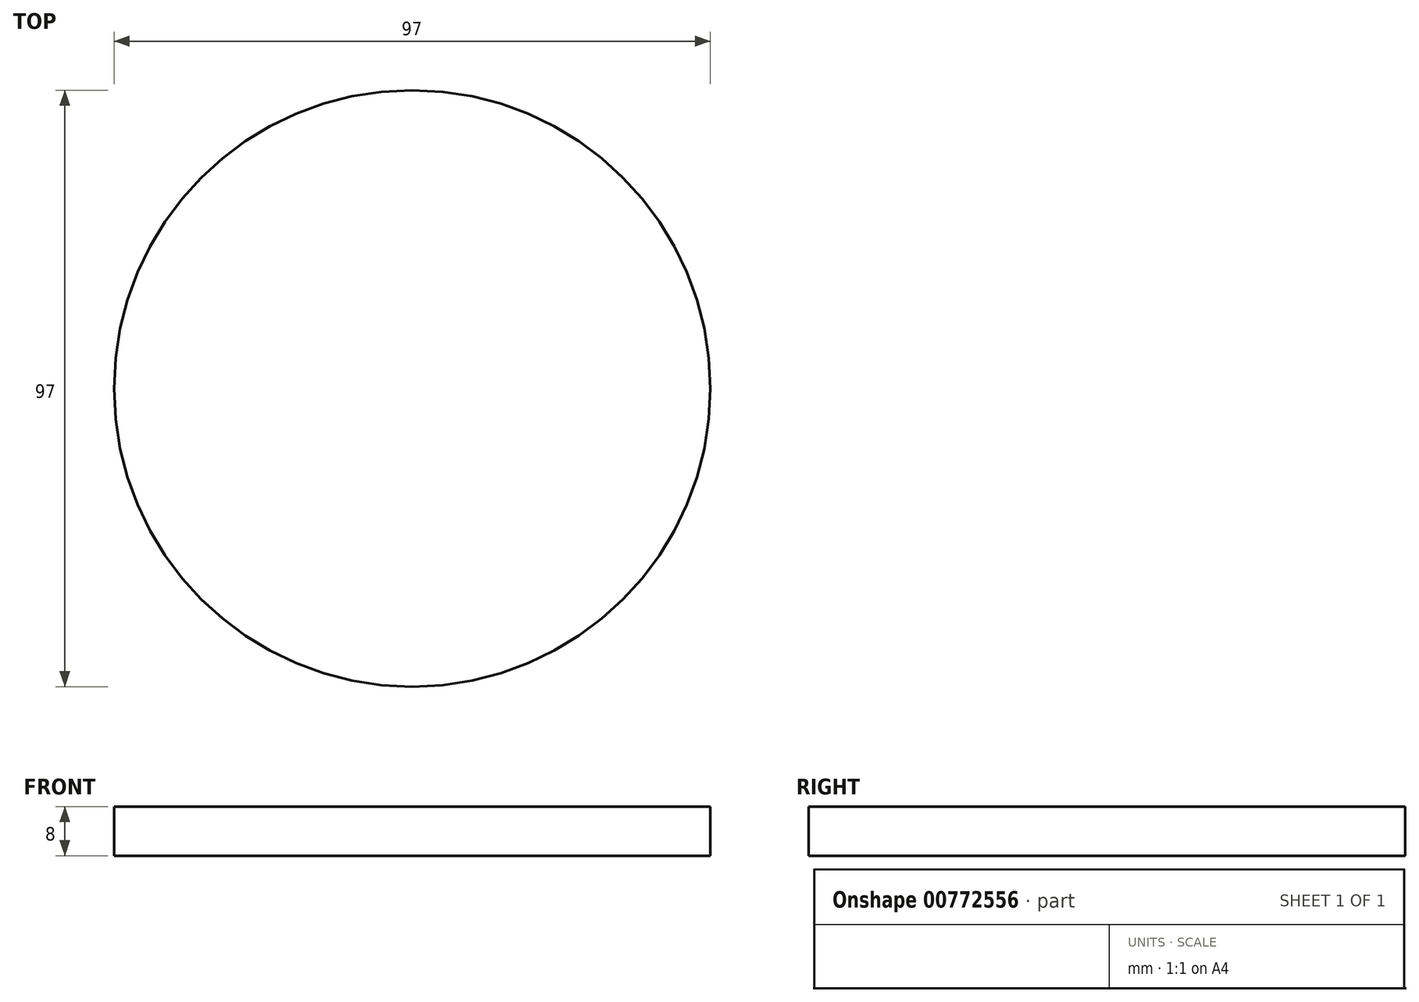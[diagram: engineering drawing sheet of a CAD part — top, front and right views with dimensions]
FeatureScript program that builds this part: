
annotation { "Feature Type Name" : "Feature", "Feature Type Description" : "" }
export const myFeature = defineFeature(function(context is Context, id is Id, definition is map)
    precondition{}
    {
        {
            var Q0;
            Q0=qCreatedBy(makeId("Top.planeOp"),FACE);
            var sketch = newSketch(context, id + "F0", { "sketchPlane" : qUnion([Q0])});
            skCircle(sketch, "E0", {"center": v(0, 0) * mm, "radius": 48.5 * mm});
            skSolve(sketch);
        }
        {
            var Q0;
            Q0=makeQuery(id+"F0.imprint","IMPRINT",FACE,{"disambiguationData":[TD([[makeQuery(id+"F0.imprint","IMPRINT",EDGE,{"derivedFrom":sQuery(id+"F0.wireOp",EDGE,"E0")}),1.0]])]});
            extrude(context, id + "F1", {"entities" : qUnion([Q0]), "depth" : 8 * mm, "offsetDistance" : 25 * mm});
        }
    });
